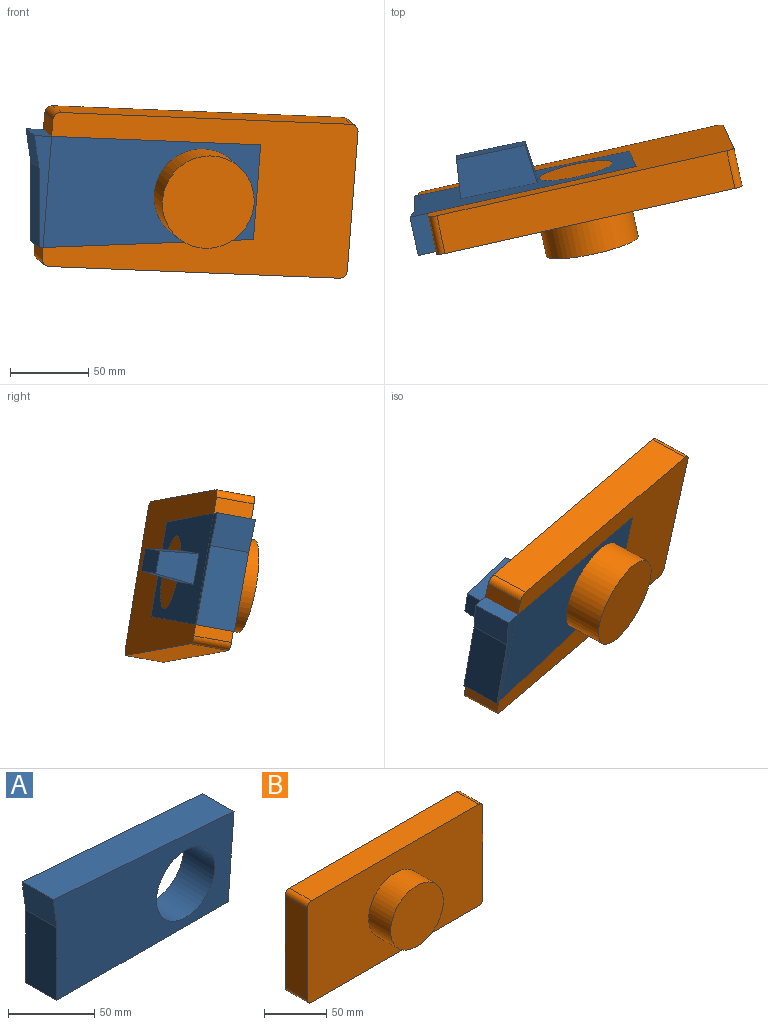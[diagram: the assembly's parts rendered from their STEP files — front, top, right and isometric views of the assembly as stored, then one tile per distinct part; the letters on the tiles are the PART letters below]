
ASSEMBLY  parts=2 mates=1
PART A: 13 faces, bbox 148x50.4x72.8 mm
  f0: plane 25.4x21.35mm, normal (-0.99,0,-0.15), area 548.2mm2, adj f1,f4,f5,f6
  f1: plane 51.46x25.4mm, normal (-1,0,0), area 1307mm2, adj f0,f2,f5,f6
  f2: plane 140.05x25.4mm, normal (0,0,-1), area 3557.3mm2, adj f1,f3,f5,f6
  f3: plane 61.31x25.4mm, normal (1,0,-0.08), area 1562mm2, adj f2,f4,f5,f6
  f4: plane 147.95x25.4mm, normal (0.08,0,1), area 3769.3mm2, adj f0,f3,f5,f6
  f5: plane 147.95x72.81mm, normal (0,-1,0), area 7801.7mm2, adj f0,f1,f2,f3,f4,f7
  f6: plane 147.95x72.81mm, normal (0,1,0), area 6801.7mm2, adj f0,f1,f2,f3,f4,f7,f8,f9
  f7: cylinder r=23.8mm len=47.6mm, axis (0,-1,0), area 3798mm2, adj f5,f6
  f8: plane 50x25mm, normal (0,0.1,0.99), area 1190.8mm2, adj f6,f9,f11,f12
  f9: plane 25x20mm, normal (0.99,0.1,0), area 436.7mm2, adj f6,f8,f10,f12
  f10: plane 50x25mm, normal (0,0.1,-0.99), area 1190.8mm2, adj f6,f9,f11,f12
  f11: plane 25x20mm, normal (-0.99,0.1,0), area 436.7mm2, adj f6,f8,f10,f12
  f12: plane 44.74x14.74mm, normal (0,1,0), area 659.8mm2, adj f8,f9,f10,f11
PART B: 12 faces, bbox 200x50x100 mm
  f0: plane 90x25mm, normal (1,0,0), area 2250mm2, adj f4,f5,f6,f9
  f1: plane 190x25mm, normal (0,0,1), area 4750mm2, adj f4,f5,f6,f7
  f2: plane 90x25mm, normal (-1,0,0), area 2250mm2, adj f4,f5,f7,f8
  f3: plane 190x25mm, normal (0,0,-1), area 4750mm2, adj f4,f5,f8,f9
  f4: plane 200x100mm, normal (0,-1,0), area 17151.1mm2, adj f0,f1,f2,f3,f6,f7,f8,f9
  f5: plane 200x100mm, normal (0,1,0), area 19978.5mm2, adj f0,f1,f2,f3,f6,f7,f8,f9
  f6: cylinder r=5mm len=25mm, axis (0,1,0), area 196.3mm2, adj f0,f1,f4,f5
  f7: cylinder r=5mm len=25mm, axis (0,-1,0), area 196.3mm2, adj f1,f2,f4,f5
  f8: cylinder r=5mm len=25mm, axis (0,1,0), area 196.3mm2, adj f2,f3,f4,f5
  f9: cylinder r=5mm len=25mm, axis (0,-1,0), area 196.3mm2, adj f0,f3,f4,f5
  f10: cylinder r=30mm len=60mm, axis (0,1,0), area 4712.4mm2, adj f4,f11
  f11: plane 60x60mm, normal (0,-1,0), area 2827.4mm2, adj f10
PLACE A rot(axis=(0.64,-0.07,0.76),15.8deg) t=(-51.44,-43.3,54.42)mm
PLACE B rot(axis=(0.6,0.21,0.77),16.1deg) t=(-31.55,-33.77,24.26)mm
MATE cylindrical B.f10 <-> A.f7  axis (-0.21,0.96,0.17) through (-23.72,-69.86,17.76)mm
